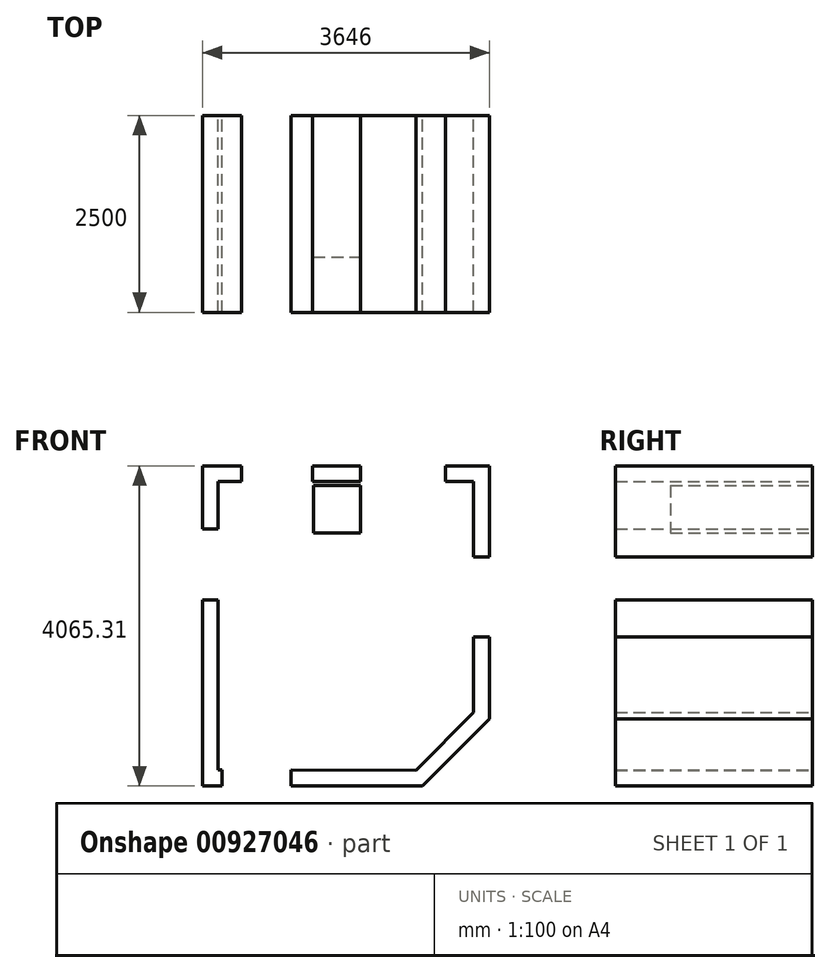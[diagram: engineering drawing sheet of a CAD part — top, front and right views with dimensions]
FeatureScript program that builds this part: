
annotation { "Feature Type Name" : "Feature", "Feature Type Description" : "" }
export const myFeature = defineFeature(function(context is Context, id is Id, definition is map)
    precondition{}
    {
        {
            var Q0;
            Q0=qCreatedBy(makeId("Front.planeOp"),FACE);
            var sketch = newSketch(context, id + "F0", { "sketchPlane" : qUnion([Q0])});
            skLineSegment(sketch, "E0", {"start": v(0, 0) * mm, "end": v(300, 0) * mm});
            skLineSegment(sketch, "E1", {"start": v(300, 0) * mm, "end": v(1200, 0) * mm, "construction": true});
            skLineSegment(sketch, "E2", {"start": v(1200, 0) * mm, "end": v(1810, 0) * mm});
            skLineSegment(sketch, "E3", {"start": v(1810, 0) * mm, "end": v(2886, 0) * mm, "construction": true});
            skLineSegment(sketch, "E4", {"start": v(2886, 0) * mm, "end": v(3246, 0) * mm});
            skLineSegment(sketch, "E5", {"start": v(3246, 0) * mm, "end": v(3246, -960) * mm});
            skLineSegment(sketch, "E6", {"start": v(3246, -960) * mm, "end": v(3246, -1974) * mm, "construction": true});
            skLineSegment(sketch, "E7", {"start": v(3246, -1974) * mm, "end": v(3246, -2934) * mm});
            skLineSegment(sketch, "E8", {"start": v(3246, -2934) * mm, "end": v(2515, -3665.3) * mm});
            skLineSegment(sketch, "E9", {"start": v(0, 0) * mm, "end": v(0, -600) * mm});
            skLineSegment(sketch, "E10", {"start": v(0, -3665) * mm, "end": v(0, -1500) * mm});
            skLineSegment(sketch, "E11", {"start": v(0, -600) * mm, "end": v(0, -1500) * mm, "construction": true});
            skLineSegment(sketch, "E12", {"start": v(2515, -3665.3) * mm, "end": v(925, -3665.1) * mm});
            skLineSegment(sketch, "E13", {"start": v(925, -3665.1) * mm, "end": v(50, -3665) * mm, "construction": true});
            skLineSegment(sketch, "E14", {"start": v(50, -3665) * mm, "end": v(0, -3665) * mm});
            skLineSegment(sketch, "E15.0", {"start": v(1200, 200) * mm, "end": v(1810, 200) * mm});
            skLineSegment(sketch, "E16.0", {"start": v(3446, 200) * mm, "end": v(3446, -960) * mm});
            skLineSegment(sketch, "E16.1", {"start": v(2886, 200) * mm, "end": v(3446, 200) * mm});
            skLineSegment(sketch, "E17.0", {"start": v(2597.86, -3865.3) * mm, "end": v(924.98, -3865.1) * mm});
            skLineSegment(sketch, "E17.1", {"start": v(3446, -3016.82) * mm, "end": v(2597.86, -3865.3) * mm});
            skLineSegment(sketch, "E17.2", {"start": v(3446, -1974) * mm, "end": v(3446, -3016.82) * mm});
            skLineSegment(sketch, "E18.0", {"start": v(-200, -3864.98) * mm, "end": v(-200, -1500) * mm});
            skLineSegment(sketch, "E18.1", {"start": v(49.98, -3865) * mm, "end": v(-200, -3864.98) * mm});
            skLineSegment(sketch, "E19.0", {"start": v(-200, 200) * mm, "end": v(300, 200) * mm});
            skLineSegment(sketch, "E19.1", {"start": v(-200, 200) * mm, "end": v(-200, -600) * mm});
            skLineSegment(sketch, "E20", {"start": v(300, 200) * mm, "end": v(300, 0) * mm});
            skLineSegment(sketch, "E21", {"start": v(-200, -600) * mm, "end": v(0, -600) * mm});
            skLineSegment(sketch, "E22", {"start": v(-200, -1500) * mm, "end": v(0, -1500) * mm});
            skLineSegment(sketch, "E23", {"start": v(49.98, -3865) * mm, "end": v(50, -3665) * mm});
            skLineSegment(sketch, "E24", {"start": v(925, -3665.1) * mm, "end": v(924.98, -3865.1) * mm});
            skLineSegment(sketch, "E25", {"start": v(3446, -1974) * mm, "end": v(3246, -1974) * mm});
            skLineSegment(sketch, "E26", {"start": v(3446, -960) * mm, "end": v(3246, -960) * mm});
            skLineSegment(sketch, "E27", {"start": v(2886, 200) * mm, "end": v(2886, 0) * mm});
            skLineSegment(sketch, "E28", {"start": v(1810, 200) * mm, "end": v(1810, 0) * mm});
            skLineSegment(sketch, "E29", {"start": v(1200, 200) * mm, "end": v(1200, 0) * mm});
            skSolve(sketch);
        }
        {
            var Q0;
            Q0 = qSketchRegion(id + "F0", true);
            extrude(context, id + "F1", {"entities" : qUnion([Q0]), "depth" : 2500 * mm, "offsetDistance" : 25 * mm});
        }
        {
            var Q0;
            Q0=qCreatedBy(makeId("Front.planeOp"),FACE);
            var sketch = newSketch(context, id + "F2", { "sketchPlane" : qUnion([Q0])});
            skLineSegment(sketch, "E30.bottom", {"start": v(1210, -50) * mm, "end": v(1810, -50) * mm});
            skLineSegment(sketch, "E30.top", {"start": v(1210, -650) * mm, "end": v(1810, -650) * mm});
            skLineSegment(sketch, "E30.left", {"start": v(1210, -50) * mm, "end": v(1210, -650) * mm});
            skLineSegment(sketch, "E30.right", {"start": v(1810, -50) * mm, "end": v(1810, -650) * mm});
            skSolve(sketch);
        }
        {
            var Q0;
            Q0 = qSketchRegion(id + "F2", true);
            extrude(context, id + "F3", {"entities" : qUnion([Q0]), "depth" : 1800 * mm, "offsetDistance" : 25 * mm});
        }
    });
